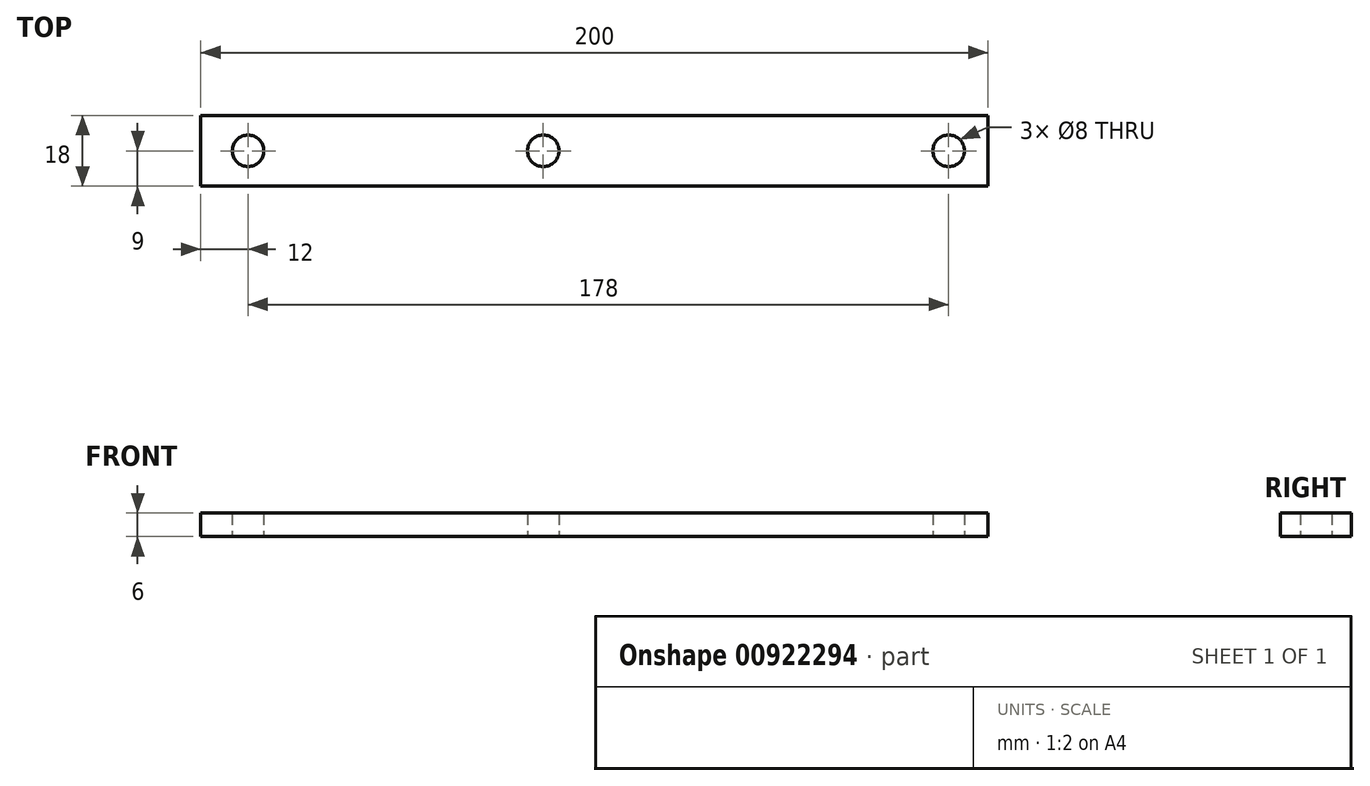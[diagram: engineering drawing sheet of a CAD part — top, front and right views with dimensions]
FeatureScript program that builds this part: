
annotation { "Feature Type Name" : "Feature", "Feature Type Description" : "" }
export const myFeature = defineFeature(function(context is Context, id is Id, definition is map)
    precondition{}
    {
        {
            var Q0;
            Q0=qCreatedBy(makeId("Top.planeOp"),FACE);
            var sketch = newSketch(context, id + "F0", { "sketchPlane" : qUnion([Q0])});
            skLineSegment(sketch, "E0.bottom", {"start": v(0, 0) * mm, "end": v(200, 0) * mm});
            skLineSegment(sketch, "E0.top", {"start": v(0, 18) * mm, "end": v(200, 18) * mm});
            skLineSegment(sketch, "E0.left", {"start": v(0, 0) * mm, "end": v(0, 18) * mm});
            skLineSegment(sketch, "E0.right", {"start": v(200, 0) * mm, "end": v(200, 18) * mm});
            skSolve(sketch);
        }
        {
            var Q0;
            Q0=makeQuery(id+"F0.imprint","IMPRINT",FACE,{"disambiguationData":[TD([[makeQuery(id+"F0.imprint","IMPRINT",EDGE,{"derivedFrom":sQuery(id+"F0.wireOp",EDGE,"E0.bottom")}),1.0]])]});
            var sketch = newSketch(context, id + "F1", { "sketchPlane" : qUnion([Q0])});
            skCircle(sketch, "E1", {"center": v(12, 9) * mm, "radius": 4 * mm});
            skCircle(sketch, "E2", {"center": v(87, 9) * mm, "radius": 4 * mm});
            skCircle(sketch, "E3", {"center": v(190, 9) * mm, "radius": 4 * mm});
            skSolve(sketch);
        }
        {
            var Q0;
            Q0=makeQuery(id+"F1.imprint","IMPRINT",FACE,{"disambiguationData":[TD([[makeQuery(id+"F1.imprint","IMPRINT",EDGE,{"derivedFrom":sQuery(id+"F1.wireOp",EDGE,"E1")}),-1.0]])]});
            extrude(context, id + "F2", {"entities" : qUnion([Q0]), "depth" : 6 * mm, "offsetDistance" : 25 * mm});
        }
    });
